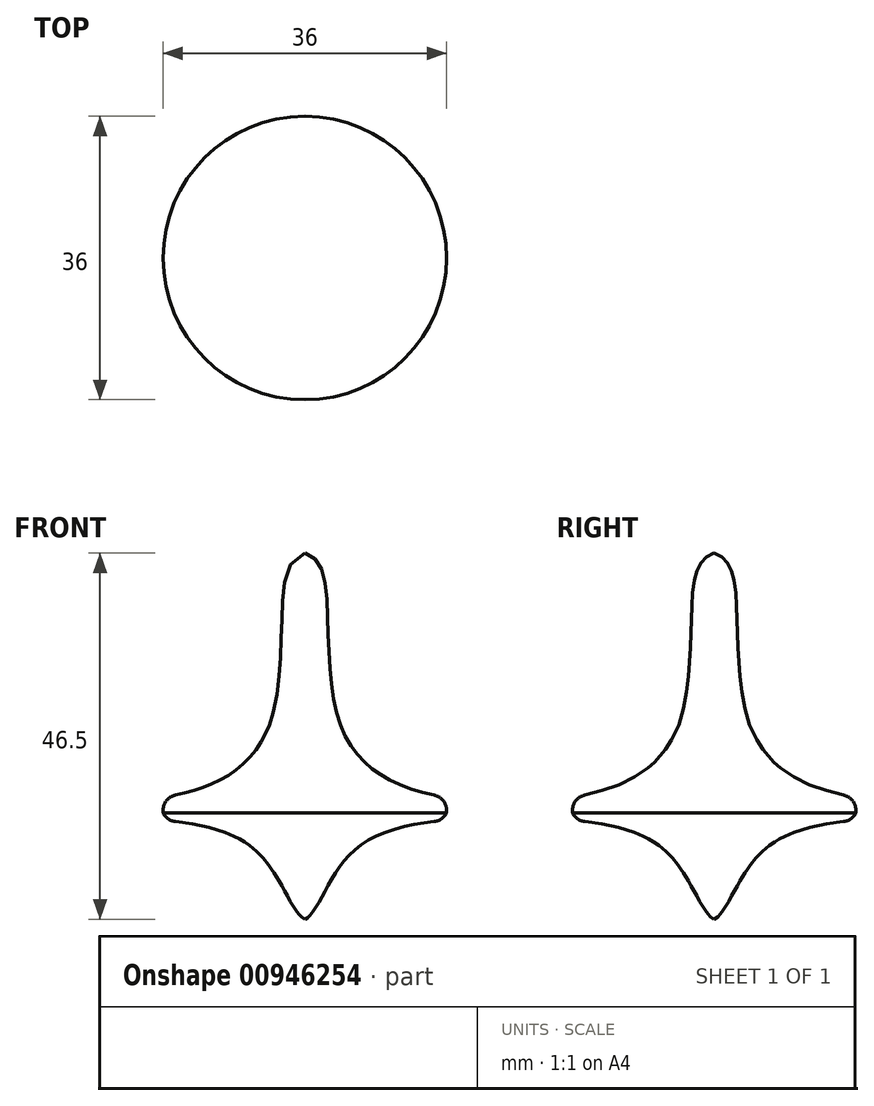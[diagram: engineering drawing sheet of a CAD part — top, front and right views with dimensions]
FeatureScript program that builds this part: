
annotation { "Feature Type Name" : "Feature", "Feature Type Description" : "" }
export const myFeature = defineFeature(function(context is Context, id is Id, definition is map)
    precondition{}
    {
        {
            var Q0;
            Q0=qCreatedBy(makeId("Front.planeOp"),FACE);
            var sketch = newSketch(context, id + "F0", { "sketchPlane" : qUnion([Q0])});
            skLineSegment(sketch, "E0", {"start": v(0, 0) * mm, "end": v(18, 0) * mm});
            skLineSegment(sketch, "E1", {"start": v(0, 0) * mm, "end": v(0, 33) * mm});
            skLineSegment(sketch, "E2", {"start": v(18, 0) * mm, "end": v(18, 2) * mm});
            skFitSpline(sketch, "E3", {"points": [v(18, 2) * mm, v(11.49, 3.85) * mm, v(7.24, 6.82) * mm, v(4.14, 12.29) * mm, v(2.92, 24.38) * mm, v(0, 33) * mm], "startDerivative": vector(-34, 4.8) * mm, "endDerivative": vector(-37.03, 8.77) * mm});
            skSolve(sketch);
        }
        {
            var Q0;
            Q0=makeQuery(id+"F0.imprint","IMPRINT",FACE,{"disambiguationData":[TD([[makeQuery(id+"F0.imprint","IMPRINT",EDGE,{"derivedFrom":sQuery(id+"F0.wireOp",EDGE,"E0")}),1.0]])]});
            var Q1;
            Q1=sQuery(id+"F0.wireOp",EDGE,"E1");
            revolve(context, id + "F1", {"surfaceOperationType" : NewSurfaceOperationType.NEW, "entities" : qUnion([Q0]), "axis" : qUnion([Q1]), "revolveType" : RevolveType.FULL});
        }
        {
            var Q0;
            Q0=qCreatedBy(makeId("Front.planeOp"),FACE);
            var sketch = newSketch(context, id + "F2", { "sketchPlane" : qUnion([Q0])});
            skLineSegment(sketch, "E4", {"start": v(0, 0) * mm, "end": v(18, 0) * mm});
            skLineSegment(sketch, "E5", {"start": v(18, 0) * mm, "end": v(18, -1) * mm});
            skLineSegment(sketch, "E6", {"start": v(0, 0) * mm, "end": v(0, -13.5) * mm});
            skFitSpline(sketch, "E7", {"points": [v(0, -13.5) * mm, v(1.2, -12.27) * mm, v(3.45, -8.37) * mm, v(7.93, -3.53) * mm, v(18, -1) * mm], "startDerivative": vector(7.45, 2) * mm, "endDerivative": vector(28.09, 0.97) * mm});
            skSolve(sketch);
        }
        {
            var Q0;
            Q0=makeQuery(id+"F2.imprint","IMPRINT",FACE,{"disambiguationData":[TD([[makeQuery(id+"F2.imprint","IMPRINT",EDGE,{"derivedFrom":sQuery(id+"F2.wireOp",EDGE,"E4")}),-1.0]])]});
            var Q1;
            Q1=sQuery(id+"F2.wireOp",EDGE,"E6");
            revolve(context, id + "F3", {"surfaceOperationType" : NewSurfaceOperationType.NEW, "entities" : qUnion([Q0]), "axis" : qUnion([Q1]), "revolveType" : RevolveType.FULL});
        }
        {
            var Q0;
            Q0=makeQuery(id+"F1.opRevolve","SWEPT_EDGE",EDGE,{"disambiguationData":[OSD([sQuery(id+"F0.wireOp",EDGE,"E2"),sQuery(id+"F0.wireOp",EDGE,"E3")])]});
            var Q1;
            Q1=makeQuery(id+"F3.opRevolve","SWEPT_EDGE",EDGE,{"disambiguationData":[OSD([sQuery(id+"F2.wireOp",EDGE,"E5"),sQuery(id+"F2.wireOp",EDGE,"E7")])]});
            fillet(context, id + "F4", {"entities" : qUnion([Q0, Q1]), "radius" : 2 * mm, "tangentPropagation" : true, "allowEdgeOverflow" : false});
        }
    });
